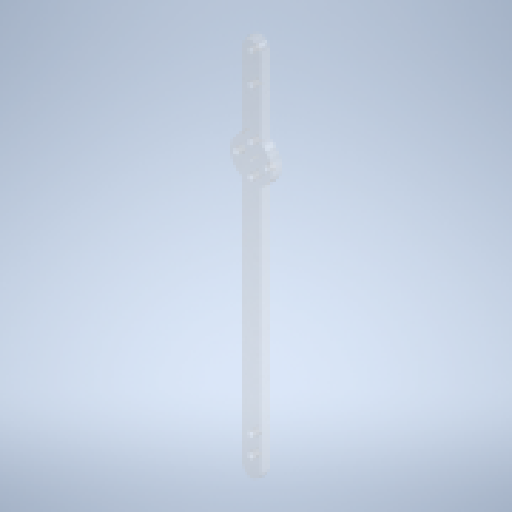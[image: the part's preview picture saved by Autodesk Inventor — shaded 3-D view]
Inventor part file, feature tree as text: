
AUTODESK INVENTOR PART (.ipt)
format: ipt  version: 2023.1 (Build 271208000, 208)  size: 301,568 bytes
history: native  units: mm
features: sketch x2, extrude x1, move_body x1
ambient origin geometry x8: Origin, YZ Plane, XZ Plane, XY Plane, X Axis, Y Axis, Z Axis, Center Point
bodies: Solid1 (feature_tree)
feature tree (4):
  extrude  "Extrusion1"  Depth=10.0mm
  move_body  "Move Body1"
  sketch  "Sketch3"  dims[d2=190.0mm d3=21.0mm d4=50.0mm d5=3.0mm d6=3.0mm d7=3.0mm d8=3.0mm d9=3.0mm d10=8.0mm d11=11.0mm d12=40.0mm d14=360.0deg d16=0.0mm d17=16.0mm d18=5.0mm d19=10.0mm d20=5.0mm d21=0.0mm d22=11.0mm d26=0.0mm d27=-140.0mm d28=0.0mm]
  sketch  "Sketch1"  dims[d0=10.0mm d1=10.0mm]
